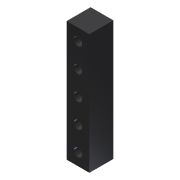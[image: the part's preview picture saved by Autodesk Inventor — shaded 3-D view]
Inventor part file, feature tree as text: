
AUTODESK INVENTOR PART (.ipt)
format: ipt  version: 2014 (Build 180170000, 170)  size: 95,232 bytes
history: native  units: in
note: dims shown in document units (in); Inventor stores cm internally (conversion verified against a paired STEP export)
features: extrude x1, sketch x1
ambient origin geometry x8: Origin, YZ Plane, XZ Plane, XY Plane, X Axis, Y Axis, Z Axis, Center Point
bodies: Solid1 (feature_tree)
feature tree (2):
  extrude  "Extrusion1"  Depth=0.5in
  sketch  "Sketch1"  dims[d0=0.095in d1=0.5in d2=0.035in d3=0.035in d4=0.035in d5=0.05in d6=0.1in d7=0.1in d8=0.035in d9=0.035in d10=0.1in d11=0.1in d12=0.0475in d13=0.1in d14=0.0in]
